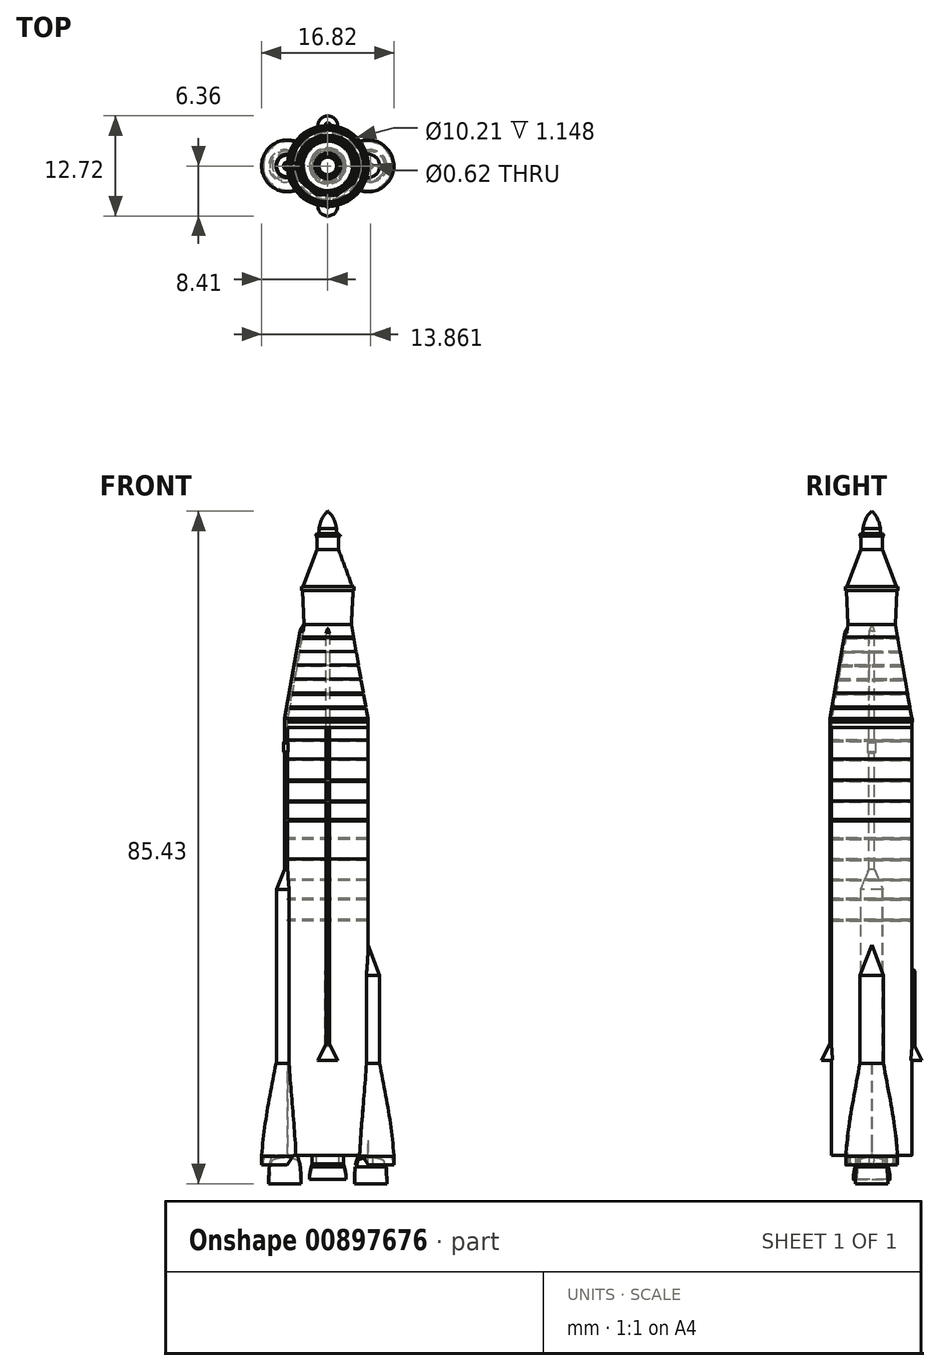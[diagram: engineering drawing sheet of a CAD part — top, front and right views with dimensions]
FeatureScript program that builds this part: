
annotation { "Feature Type Name" : "Feature", "Feature Type Description" : "" }
export const myFeature = defineFeature(function(context is Context, id is Id, definition is map)
    precondition{}
    {
        {
            var Q0;
            Q0=qCreatedBy(makeId("Front.planeOp"),FACE);
            var sketch = newSketch(context, id + "F0", { "sketchPlane" : qUnion([Q0])});
            skFitSpline(sketch, "E0", {"points": [v(0, 33.25) * mm, v(-0.75, 32.29) * mm, v(-1.12, 31.04) * mm, v(-1.14, 31.02) * mm, v(-1.13, 31.02) * mm], "startDerivative": vector(-1.93, -1.75) * mm, "endDerivative": vector(0, -10.34) * mm});
            skLineSegment(sketch, "E1", {"start": v(-1.12, 31.04) * mm, "end": v(-1.12, 30.38) * mm});
            skLineSegment(sketch, "E2", {"start": v(-1.12, 30.38) * mm, "end": v(-1.36, 30.38) * mm});
            skLineSegment(sketch, "E3", {"start": v(-1.36, 30.38) * mm, "end": v(-1.62, 30.09) * mm});
            skLineSegment(sketch, "E4", {"start": v(-1.62, 30.09) * mm, "end": v(-1.36, 30.09) * mm});
            skLineSegment(sketch, "E5", {"start": v(-1.36, 30.09) * mm, "end": v(-1.36, 28.36) * mm});
            skLineSegment(sketch, "E6", {"start": v(-1.36, 28.36) * mm, "end": v(-3.13, 23.65) * mm});
            skLineSegment(sketch, "E7", {"start": v(-3.13, 23.65) * mm, "end": v(-3.34, 23.65) * mm});
            skLineSegment(sketch, "E8", {"start": v(-3.34, 23.65) * mm, "end": v(-3.34, 23.17) * mm});
            skLineSegment(sketch, "E9", {"start": v(-3.34, 23.17) * mm, "end": v(-3.22, 23.17) * mm});
            skLineSegment(sketch, "E10", {"start": v(-3.22, 23.17) * mm, "end": v(-3, 18.86) * mm});
            skLineSegment(sketch, "E11", {"start": v(-3, 18.86) * mm, "end": v(-5.1, 6.9) * mm});
            skLineSegment(sketch, "E12", {"start": v(-5.1, 6.9) * mm, "end": v(-5.1, -46.68) * mm});
            skLineSegment(sketch, "E13", {"start": v(0, 33.25) * mm, "end": v(0, -46.63) * mm});
            skLineSegment(sketch, "E14", {"start": v(0, -46.63) * mm, "end": v(0, -46.68) * mm});
            skLineSegment(sketch, "E15", {"start": v(0, -46.72) * mm, "end": v(0, -46.68) * mm});
            skLineSegment(sketch, "E16", {"start": v(0, -46.72) * mm, "end": v(0, -48.6) * mm});
            skLineSegment(sketch, "E17", {"start": v(0, -48.6) * mm, "end": v(-5.1, -48.6) * mm});
            skLineSegment(sketch, "E18", {"start": v(-5.1, -48.6) * mm, "end": v(-5.1, -46.69) * mm});
            skLineSegment(sketch, "E19", {"start": v(-5.1, -46.69) * mm, "end": v(-5.1, -46.68) * mm});
            skLineSegment(sketch, "E20", {"start": v(0, 0) * mm, "end": v(0, 54.61) * mm});
            skLineSegment(sketch, "E21", {"start": v(0, 54.61) * mm, "end": v(-49.9, 54.61) * mm});
            skLineSegment(sketch, "E22", {"start": v(-35.1, 47.93) * mm, "end": v(-34.7, 47.5) * mm});
            skLineSegment(sketch, "E23", {"start": v(50.7, 54.83) * mm, "end": v(50.65, 54.64) * mm});
            skLineSegment(sketch, "E24", {"start": v(-35.08, -48.61) * mm, "end": v(45, -48.61) * mm});
            skLineSegment(sketch, "E25", {"start": v(-35.08, -48.61) * mm, "end": v(-56.76, -48.61) * mm});
            skLineSegment(sketch, "E26", {"start": v(0, -46.68) * mm, "end": v(0, -48.61) * mm});
            skFitSpline(sketch, "E27", {"points": [v(-3.23, -48.61) * mm, v(-2.86, -45) * mm, v(-1.42, -36.8) * mm], "startDerivative": vector(0.63, 8.16) * mm, "endDerivative": vector(2.85, 15) * mm});
            skLineSegment(sketch, "E28", {"start": v(-1.42, -36.8) * mm, "end": v(0, -36.8) * mm});
            skLineSegment(sketch, "E29", {"start": v(0, -36.8) * mm, "end": v(0, -48.61) * mm});
            skLineSegment(sketch, "E30", {"start": v(-3.23, -48.61) * mm, "end": v(-3.23, -49.7) * mm});
            skLineSegment(sketch, "E31", {"start": v(-3.23, -49.7) * mm, "end": v(0, -49.7) * mm});
            skLineSegment(sketch, "E32", {"start": v(0, -49.7) * mm, "end": v(0, -49.67) * mm});
            skLineSegment(sketch, "E33", {"start": v(28.34, 54.64) * mm, "end": v(0, 54.64) * mm});
            skLineSegment(sketch, "E34", {"start": v(0, 54.64) * mm, "end": v(0, 0.05) * mm});
            skLineSegment(sketch, "E35", {"start": v(-21.54, 19.8) * mm, "end": v(2.52, 19.8) * mm});
            skLineSegment(sketch, "E36", {"start": v(-3.04, 19.8) * mm, "end": v(-3.13, 19.53) * mm});
            skLineSegment(sketch, "E37", {"start": v(-5.48, -12.23) * mm, "end": v(-5.48, 6.9) * mm});
            skLineSegment(sketch, "E38", {"start": v(-5.48, 6.9) * mm, "end": v(-3.37, 18.82) * mm});
            skLineSegment(sketch, "E39", {"start": v(-3.37, 18.82) * mm, "end": v(-3.13, 19.53) * mm});
            skLineSegment(sketch, "E40", {"start": v(-5.48, -12.23) * mm, "end": v(-6.5, -14.79) * mm});
            skLineSegment(sketch, "E41", {"start": v(-6.5, -14.79) * mm, "end": v(-6.5, -38.04) * mm});
            skLineSegment(sketch, "E42", {"start": v(-8.4, -49.8) * mm, "end": v(-5.14, -49.8) * mm});
            skLineSegment(sketch, "E43", {"start": v(-5.14, -49.8) * mm, "end": v(-4.4, -48.61) * mm});
            skLineSegment(sketch, "E44", {"start": v(-4.4, -48.61) * mm, "end": v(-5.1, -36.81) * mm});
            skLineSegment(sketch, "E45", {"start": v(-5.48, -12.23) * mm, "end": v(-5.1, -12.23) * mm});
            skLineSegment(sketch, "E46", {"start": v(-5.1, -36.81) * mm, "end": v(-5.14, -49.8) * mm});
            skLineSegment(sketch, "E47", {"start": v(-5.48, 6.9) * mm, "end": v(-5.1, 6.9) * mm});
            skLineSegment(sketch, "E48", {"start": v(-3.51, 18) * mm, "end": v(-3, 18.86) * mm});
            skLineSegment(sketch, "E49", {"start": v(-8.25, -49.8) * mm, "end": v(-8.18, -48.61) * mm});
            skLineSegment(sketch, "E50", {"start": v(-6.5, -38.04) * mm, "end": v(-5.1, -38.04) * mm});
            skFitSpline(sketch, "E51", {"points": [v(-8.4, -48.71) * mm, v(-8.04, -45.11) * mm, v(-6.6, -36.9) * mm], "startDerivative": vector(0.63, 8.16) * mm, "endDerivative": vector(2.85, 15) * mm});
            skLineSegment(sketch, "E52", {"start": v(-6.6, -36.9) * mm, "end": v(-5.17, -36.9) * mm});
            skLineSegment(sketch, "E53", {"start": v(-8.4, -48.71) * mm, "end": v(-8.4, -49.8) * mm});
            skLineSegment(sketch, "E54", {"start": v(-8.4, -49.8) * mm, "end": v(-5.17, -49.8) * mm});
            skLineSegment(sketch, "E55", {"start": v(-6.6, -36.9) * mm, "end": v(-6.5, -36) * mm});
            skLineSegment(sketch, "E56", {"start": v(-5.14, -49.8) * mm, "end": v(-5.14, -50.06) * mm});
            skLineSegment(sketch, "E57", {"start": v(-5.14, -50.06) * mm, "end": v(-1.45, -50.06) * mm});
            skLineSegment(sketch, "E58", {"start": v(-1.45, -50.06) * mm, "end": v(-1.45, -48.6) * mm});
            skFitSpline(sketch, "E59.MirrorCS", {"points": [v(8.4, -48.71) * mm, v(8.04, -45.11) * mm, v(6.6, -36.9) * mm], "startDerivative": vector(-0.63, 8.16) * mm, "endDerivative": vector(-2.85, 15) * mm});
            skLineSegment(sketch, "E60.MirrorCS", {"start": v(8.4, -48.71) * mm, "end": v(8.4, -49.8) * mm});
            skLineSegment(sketch, "E61.MirrorCS", {"start": v(8.4, -49.8) * mm, "end": v(5.14, -49.8) * mm});
            skLineSegment(sketch, "E62.MirrorCS", {"start": v(5.1, 6.9) * mm, "end": v(5.1, -46.68) * mm});
            skLineSegment(sketch, "E63", {"start": v(6.6, -36.9) * mm, "end": v(6.6, -25.72) * mm});
            skLineSegment(sketch, "E64", {"start": v(6.6, -25.72) * mm, "end": v(5.1, -21.85) * mm});
            skLineSegment(sketch, "E65", {"start": v(5.14, -49.8) * mm, "end": v(5.1, -46.68) * mm});
            skLineSegment(sketch, "E66.MirrorCS", {"start": v(8.25, -49.8) * mm, "end": v(8.18, -48.61) * mm});
            skLineSegment(sketch, "E67.MirrorCS", {"start": v(5.14, -49.8) * mm, "end": v(4.4, -48.61) * mm});
            skLineSegment(sketch, "E68.MirrorCS", {"start": v(5.14, -50.06) * mm, "end": v(1.45, -50.06) * mm});
            skLineSegment(sketch, "E69.MirrorCS", {"start": v(5.14, -49.8) * mm, "end": v(5.14, -50.06) * mm});
            skLineSegment(sketch, "E70.MirrorCS", {"start": v(1.45, -50.06) * mm, "end": v(1.45, -48.6) * mm});
            skLineSegment(sketch, "E71", {"start": v(3.4, -52.18) * mm, "end": v(7.5, -52.18) * mm});
            skFitSpline(sketch, "E72", {"points": [v(3.4, -52.18) * mm, v(3.46, -50.24) * mm, v(3.65, -49.24) * mm, v(3.86, -48.61) * mm, v(3.86, -48.61) * mm], "startDerivative": vector(0.05, 4.96) * mm, "endDerivative": vector(0.02, -0.01) * mm});
            skLineSegment(sketch, "E73", {"start": v(5.45, -52.18) * mm, "end": v(5.45, -48.61) * mm});
            skFitSpline(sketch, "E74", {"points": [v(3.59, -52.18) * mm, v(3.65, -50.23) * mm, v(3.81, -49.3) * mm, v(3.9, -49.17) * mm], "startDerivative": vector(0.01, 4.02) * mm, "endDerivative": vector(0.64, 0.62) * mm});
            skFitSpline(sketch, "E75", {"points": [v(3.9, -49.17) * mm, v(4.06, -49.08) * mm, v(4.96, -48.85) * mm, v(5.45, -48.82) * mm, v(5.45, -48.82) * mm], "startDerivative": vector(0.6, 0.45) * mm, "endDerivative": vector(-0.02, -0.05) * mm});
            skLineSegment(sketch, "E76", {"start": v(3.86, -48.61) * mm, "end": v(8.4, -48.61) * mm});
            skLineSegment(sketch, "E77.MirrorCS", {"start": v(-5.45, -52.18) * mm, "end": v(-5.45, -48.61) * mm});
            skFitSpline(sketch, "E78.MirrorCS", {"points": [v(-3.4, -52.18) * mm, v(-3.46, -50.24) * mm, v(-3.65, -49.24) * mm, v(-3.86, -48.61) * mm, v(-3.86, -48.61) * mm], "startDerivative": vector(-0.05, 4.96) * mm, "endDerivative": vector(-0.02, -0.01) * mm});
            skFitSpline(sketch, "E79.MirrorCS", {"points": [v(-3.59, -52.18) * mm, v(-3.65, -50.23) * mm, v(-3.81, -49.3) * mm, v(-3.9, -49.17) * mm], "startDerivative": vector(-0.01, 4.02) * mm, "endDerivative": vector(-0.64, 0.62) * mm});
            skLineSegment(sketch, "E80.MirrorCS", {"start": v(-3.4, -52.18) * mm, "end": v(-7.5, -52.18) * mm});
            skFitSpline(sketch, "E81.MirrorCS", {"points": [v(-3.9, -49.17) * mm, v(-4.06, -49.08) * mm, v(-4.96, -48.85) * mm, v(-5.45, -48.82) * mm, v(-5.45, -48.82) * mm], "startDerivative": vector(-0.6, 0.45) * mm, "endDerivative": vector(0.02, -0.05) * mm});
            skLineSegment(sketch, "E82", {"start": v(1.98, -48.61) * mm, "end": v(1.98, -49.64) * mm});
            skLineSegment(sketch, "E83", {"start": v(-1.84, -51.64) * mm, "end": v(2.34, -51.64) * mm});
            skFitSpline(sketch, "E84", {"points": [v(1.98, -49.64) * mm, v(2.06, -49.88) * mm, v(2.26, -50.7) * mm, v(2.34, -51.64) * mm], "startDerivative": vector(0.37, -0.95) * mm, "endDerivative": vector(0.09, -2.27) * mm});
            skFitSpline(sketch, "E85", {"points": [v(2.26, -51.64) * mm, v(2.25, -51.34) * mm, v(2.08, -50.5) * mm, v(1.67, -49.82) * mm, v(0, -49.4) * mm], "startDerivative": vector(0.02, 1.75) * mm, "endDerivative": vector(-5.55, 0.73) * mm});
            skLineSegment(sketch, "E86", {"start": v(0, -48.26) * mm, "end": v(0, -55.58) * mm});
            skLineSegment(sketch, "E87", {"start": v(0, -49.4) * mm, "end": v(0, -49.4) * mm});
            skLineSegment(sketch, "E88", {"start": v(-5.1, 3.49) * mm, "end": v(-5.73, 3.49) * mm});
            skLineSegment(sketch, "E89", {"start": v(-5.73, 2.7) * mm, "end": v(-5.1, 2.7) * mm});
            skLineSegment(sketch, "E90", {"start": v(-5.62, 3.49) * mm, "end": v(-5.62, 2.7) * mm});
            skLineSegment(sketch, "E91", {"start": v(-5.62, 3.49) * mm, "end": v(-5.62, 3.8) * mm});
            skLineSegment(sketch, "E92", {"start": v(-5.62, 3.8) * mm, "end": v(-5.1, 3.8) * mm});
            skLineSegment(sketch, "E93", {"start": v(-5.62, 2.7) * mm, "end": v(-5.48, 2.44) * mm});
            skLineSegment(sketch, "E94", {"start": v(-5.62, 3.8) * mm, "end": v(-5.48, 4.03) * mm});
            skSolve(sketch);
        }
        {
            var Q0;
            Q0=qCreatedBy(makeId("Right.planeOp"),FACE);
            var sketch = newSketch(context, id + "F1", { "sketchPlane" : qUnion([Q0])});
            skLineSegment(sketch, "E95", {"start": v(50.7, 54.78) * mm, "end": v(50.64, 54.59) * mm});
            skLineSegment(sketch, "E96", {"start": v(-35.08, -48.66) * mm, "end": v(45, -48.66) * mm});
            skLineSegment(sketch, "E97", {"start": v(-35.08, -48.66) * mm, "end": v(-56.76, -48.66) * mm});
            skLineSegment(sketch, "E98", {"start": v(0, -46.73) * mm, "end": v(0, -48.66) * mm});
            skFitSpline(sketch, "E99", {"points": [v(-3.24, -48.66) * mm, v(-2.87, -45.06) * mm, v(-1.42, -36.84) * mm], "startDerivative": vector(0.63, 8.16) * mm, "endDerivative": vector(2.85, 15) * mm});
            skLineSegment(sketch, "E100", {"start": v(-1.42, -36.84) * mm, "end": v(0, -36.84) * mm});
            skLineSegment(sketch, "E101", {"start": v(0, -36.84) * mm, "end": v(0, -48.66) * mm});
            skLineSegment(sketch, "E102", {"start": v(0, -48.66) * mm, "end": v(0, -49.72) * mm});
            skLineSegment(sketch, "E103", {"start": v(-3.24, -48.66) * mm, "end": v(-3.24, -49.75) * mm});
            skLineSegment(sketch, "E104", {"start": v(-3.24, -49.75) * mm, "end": v(0, -49.75) * mm});
            skLineSegment(sketch, "E105", {"start": v(0, -49.75) * mm, "end": v(0, -49.72) * mm});
            skLineSegment(sketch, "E106", {"start": v(49.87, 54.6) * mm, "end": v(0, 54.6) * mm});
            skLineSegment(sketch, "E107", {"start": v(0, 54.6) * mm, "end": v(0, 0) * mm});
            skSolve(sketch);
        }
        {
            var Q0;
            {var subQ9=sQuery(id+"F0.wireOp",EDGE,"E11");Q0=makeQuery(id+"F0.imprint","IMPRINT",FACE,{"disambiguationData":[TD([[makeQuery(id+"F0.imprint","IMPRINT",EDGE,{"derivedFrom":subQ9}),1.0]])]});}
            var Q1;
            {var subQ1=sQuery(id+"F0.wireOp",EDGE,"E14");Q1=makeQuery(id+"F0.imprint","IMPRINT",FACE,{"disambiguationData":[TD([[makeQuery(id+"F0.imprint","IMPRINT",EDGE,{"derivedFrom":subQ1}),-1.0]])]});}
            var Q2;
            {var subQ6=sQuery(id+"F0.wireOp",EDGE,"E1");Q2=makeQuery(id+"F0.imprint","IMPRINT",FACE,{"disambiguationData":[TD([[makeQuery(id+"F0.imprint","IMPRINT",EDGE,{"derivedFrom":subQ6}),1.0]])]});}
            var Q3;
            {var subQ0=sQuery(id+"F0.wireOp",EDGE,"E18");Q3=makeQuery(id+"F0.imprint","IMPRINT",FACE,{"disambiguationData":[TD([[makeQuery(id+"F0.imprint","IMPRINT",EDGE,{"derivedFrom":subQ0}),-1.0]])]});}
            var Q4;
            Q4=sQuery(id+"F0.wireOp",EDGE,"E13");
            revolve(context, id + "F2", {"surfaceOperationType" : NewSurfaceOperationType.NEW, "entities" : qUnion([Q0, Q1, Q2, Q3]), "axis" : qUnion([Q4]), "revolveType" : RevolveType.FULL});
        }
        {
            var Q0;
            {var subQ5=sQuery(id+"F0.wireOp",EDGE,"E24");var subQ6=makeQuery(id+"F0.imprint","INTERSECT",VERTEX,{"derivedFrom":[subQ5,sQuery(id+"F0.wireOp",EDGE,"E49")]});Q0=makeQuery(id+"F0.imprint","IMPRINT",FACE,{"disambiguationData":[TD([[makeQuery(id+"F0.imprint","IMPRINT",EDGE,{"disambiguationData":[TD([[subQ6,1.0]])],"derivedFrom":subQ5}),1.0]])]});}
            var Q1;
            {var subQ3=sQuery(id+"F0.wireOp",EDGE,"E40");Q1=makeQuery(id+"F0.imprint","IMPRINT",FACE,{"disambiguationData":[TD([[makeQuery(id+"F0.imprint","IMPRINT",EDGE,{"derivedFrom":subQ3}),1.0]])]});}
            var Q2;
            {var subQ4=sQuery(id+"F0.wireOp",EDGE,"E49");Q2=makeQuery(id+"F0.imprint","IMPRINT",FACE,{"disambiguationData":[TD([[makeQuery(id+"F0.imprint","IMPRINT",EDGE,{"derivedFrom":subQ4}),1.0]])]});}
            var Q3;
            {var subQ5=sQuery(id+"F0.wireOp",EDGE,"eI0OFrzm-inzm-73C8-oKcD-yxVDyEnJwxOV");Q3=makeQuery(id+"F0.imprint","IMPRINT",FACE,{"disambiguationData":[TD([[makeQuery(id+"F0.imprint","IMPRINT",EDGE,{"derivedFrom":subQ5}),1.0]])]});}
            var Q4;
            {var subQ5=sQuery(id+"F0.wireOp",EDGE,"E90");Q4=makeQuery(id+"F0.imprint","IMPRINT",FACE,{"disambiguationData":[TD([[makeQuery(id+"F0.imprint","IMPRINT",EDGE,{"derivedFrom":subQ5}),1.0]])]});}
            var Q5;
            {var subQ5=sQuery(id+"F0.wireOp",EDGE,"E91");Q5=makeQuery(id+"F0.imprint","IMPRINT",FACE,{"disambiguationData":[TD([[makeQuery(id+"F0.imprint","IMPRINT",EDGE,{"derivedFrom":subQ5}),-1.0]])]});}
            var Q6;
            {var subQ0=sQuery(id+"F0.wireOp",EDGE,"E47");Q6=makeQuery(id+"F0.imprint","IMPRINT",FACE,{"disambiguationData":[TD([[makeQuery(id+"F0.imprint","IMPRINT",EDGE,{"derivedFrom":subQ0}),-1.0]])]});}
            var Q7;
            {var subQ0=sQuery(id+"F0.wireOp",EDGE,"E45");Q7=makeQuery(id+"F0.imprint","IMPRINT",FACE,{"disambiguationData":[TD([[makeQuery(id+"F0.imprint","IMPRINT",EDGE,{"derivedFrom":subQ0}),1.0]])]});}
            var Q8;
            {var subQ0=sQuery(id+"F0.wireOp",EDGE,"E88");var subQ1=sQuery(id+"F0.wireOp",EDGE,"E12");var subQ2=makeQuery(id+"F0.imprint","INTERSECT",VERTEX,{"derivedFrom":[subQ1,subQ0]});Q8=makeQuery(id+"F0.imprint","IMPRINT",FACE,{"disambiguationData":[TD([[makeQuery(id+"F0.imprint","IMPRINT",EDGE,{"disambiguationData":[TD([[subQ2,-1.0]])],"derivedFrom":subQ1}),-1.0]])]});}
            var Q9;
            {var subQ0=sQuery(id+"F0.wireOp",EDGE,"E88");var subQ1=sQuery(id+"F0.wireOp",EDGE,"E12");var subQ2=makeQuery(id+"F0.imprint","INTERSECT",VERTEX,{"derivedFrom":[subQ1,subQ0]});Q9=makeQuery(id+"F0.imprint","IMPRINT",FACE,{"disambiguationData":[TD([[makeQuery(id+"F0.imprint","IMPRINT",EDGE,{"disambiguationData":[TD([[subQ2,1.0]])],"derivedFrom":subQ1}),-1.0]])]});}
            var Q10;
            {var subQ0=sQuery(id+"F0.wireOp",EDGE,"E94");Q10=makeQuery(id+"F0.imprint","IMPRINT",FACE,{"disambiguationData":[TD([[makeQuery(id+"F0.imprint","IMPRINT",EDGE,{"derivedFrom":subQ0}),-1.0]])]});}
            var Q11;
            {var subQ0=sQuery(id+"F0.wireOp",EDGE,"E93");Q11=makeQuery(id+"F0.imprint","IMPRINT",FACE,{"disambiguationData":[TD([[makeQuery(id+"F0.imprint","IMPRINT",EDGE,{"derivedFrom":subQ0}),1.0]])]});}
            var Q12;
            Q12=sQuery(id+"F0.wireOp",EDGE,"E12");
            revolve(context, id + "F3", {"operationType" : NewBodyOperationType.ADD, "surfaceOperationType" : NewSurfaceOperationType.NEW, "entities" : qUnion([Q0, Q1, Q2, Q3, Q4, Q5, Q6, Q7, Q8, Q9, Q10, Q11]), "axis" : qUnion([Q12]), "revolveType" : RevolveType.FULL});
        }
        {
            var Q0;
            Q0=qCreatedBy(makeId("Front.planeOp"),FACE);
            var sketch = newSketch(context, id + "F4", { "sketchPlane" : qUnion([Q0])});
            skLineSegment(sketch, "E108", {"start": v(-5.15, -49.8) * mm, "end": v(-4.38, -48.6) * mm});
            skLineSegment(sketch, "E109", {"start": v(-4.38, -48.6) * mm, "end": v(-1.71, -48.6) * mm});
            skLineSegment(sketch, "E110", {"start": v(-1.71, -48.6) * mm, "end": v(-1.71, -49.88) * mm});
            skLineSegment(sketch, "E111", {"start": v(-1.71, -49.88) * mm, "end": v(-5.15, -49.8) * mm});
            skLineSegment(sketch, "E112", {"start": v(-5.15, -49.8) * mm, "end": v(-5.15, -49.89) * mm});
            skLineSegment(sketch, "E113", {"start": v(-5.15, -49.89) * mm, "end": v(-1.71, -49.88) * mm});
            skSolve(sketch);
        }
        {
            var Q0;
            Q0 = qSketchRegion(id + "F4", true);
            extrude(context, id + "F5", {"entities" : qUnion([Q0]), "operationType" : NewBodyOperationType.REMOVE, "depth" : 10.24 * mm, "offsetDistance" : 25.4 * mm, "hasSecondDirection" : true, "secondDirectionOppositeDirection" : true, "secondDirectionDepth" : 25.4 * mm});
        }
        {
            var Q0;
            {var subQ4=sQuery(id+"F0.wireOp",EDGE,"E63");Q0=makeQuery(id+"F0.imprint","IMPRINT",FACE,{"disambiguationData":[TD([[makeQuery(id+"F0.imprint","IMPRINT",EDGE,{"derivedFrom":subQ4}),1.0]])]});}
            var Q1;
            {var subQ0=sQuery(id+"F0.wireOp",EDGE,"E60.MirrorCS");Q1=makeQuery(id+"F0.imprint","IMPRINT",FACE,{"disambiguationData":[TD([[makeQuery(id+"F0.imprint","IMPRINT",EDGE,{"derivedFrom":subQ0}),-1.0]])]});}
            var Q2;
            Q2=sQuery(id+"F0.wireOp",EDGE,"E62.MirrorCS");
            revolve(context, id + "F6", {"operationType" : NewBodyOperationType.ADD, "surfaceOperationType" : NewSurfaceOperationType.NEW, "entities" : qUnion([Q0, Q1]), "axis" : qUnion([Q2]), "revolveType" : RevolveType.FULL});
        }
        {
            var Q0;
            {var subQ1=sQuery(id+"F0.wireOp",EDGE,"E67.MirrorCS");Q0=makeQuery(id+"F0.imprint","IMPRINT",FACE,{"disambiguationData":[TD([[makeQuery(id+"F0.imprint","IMPRINT",EDGE,{"derivedFrom":subQ1}),1.0]])]});}
            var Q1;
            {var subQ5=sQuery(id+"F0.wireOp",EDGE,"E76");var subQ9=sQuery(id+"F0.wireOp",EDGE,"E67.MirrorCS");var subQ10=makeQuery(id+"F0.imprint","INTERSECT",VERTEX,{"derivedFrom":[subQ9,subQ5]});Q1=makeQuery(id+"F0.imprint","IMPRINT",FACE,{"disambiguationData":[TD([[makeQuery(id+"F0.imprint","IMPRINT",EDGE,{"disambiguationData":[TD([[subQ10,1.0]])],"derivedFrom":subQ9}),1.0]])]});}
            var Q2;
            {var subQ3=sQuery(id+"F0.wireOp",EDGE,"E70.MirrorCS");var subQ5=sQuery(id+"F0.wireOp",EDGE,"E68.MirrorCS");var subQ7=makeQuery(id+"F0.imprint","INTERSECT",VERTEX,{"derivedFrom":[subQ5,subQ3]});Q2=makeQuery(id+"F0.imprint","IMPRINT",FACE,{"disambiguationData":[TD([[makeQuery(id+"F0.imprint","IMPRINT",EDGE,{"disambiguationData":[TD([[subQ7,1.0]])],"derivedFrom":subQ5}),-1.0]])]});}
            var Q3;
            {var subQ0=sQuery(id+"F0.wireOp",EDGE,"E82");Q3=makeQuery(id+"F0.imprint","IMPRINT",FACE,{"disambiguationData":[TD([[makeQuery(id+"F0.imprint","IMPRINT",EDGE,{"derivedFrom":subQ0}),1.0]])]});}
            var Q4;
            {var subQ0=sQuery(id+"F0.wireOp",EDGE,"E82");Q4=makeQuery(id+"F0.imprint","IMPRINT",FACE,{"disambiguationData":[TD([[makeQuery(id+"F0.imprint","IMPRINT",EDGE,{"derivedFrom":subQ0}),-1.0]])]});}
            extrude(context, id + "F7", {"entities" : qUnion([Q0, Q1, Q2, Q3, Q4]), "operationType" : NewBodyOperationType.REMOVE, "oppositeDirection" : true, "depth" : 25.4 * mm, "offsetDistance" : 25.4 * mm, "hasSecondDirection" : true, "secondDirectionOppositeDirection" : false, "secondDirectionDepth" : 25.93 * mm});
        }
        {
            var Q0;
            {var subQ0=sQuery(id+"F0.wireOp",EDGE,"E76");var subQ1=sQuery(id+"F0.wireOp",EDGE,"E65");var subQ2=makeQuery(id+"F0.imprint","INTERSECT",VERTEX,{"derivedFrom":[subQ1,subQ0]});Q0=makeQuery(id+"F0.imprint","IMPRINT",FACE,{"disambiguationData":[TD([[makeQuery(id+"F0.imprint","IMPRINT",EDGE,{"disambiguationData":[TD([[subQ2,1.0]])],"derivedFrom":subQ1}),-1.0]])]});}
            var Q1;
            {var subQ0=sQuery(id+"F0.wireOp",EDGE,"E76");var subQ1=sQuery(id+"F0.wireOp",EDGE,"E65");var subQ2=makeQuery(id+"F0.imprint","INTERSECT",VERTEX,{"derivedFrom":[subQ1,subQ0]});Q1=makeQuery(id+"F0.imprint","IMPRINT",FACE,{"disambiguationData":[TD([[makeQuery(id+"F0.imprint","IMPRINT",EDGE,{"disambiguationData":[TD([[subQ2,1.0]])],"derivedFrom":subQ1}),1.0]])]});}
            var Q2;
            {var subQ5=sQuery(id+"F0.wireOp",EDGE,"E76");var subQ9=sQuery(id+"F0.wireOp",EDGE,"E67.MirrorCS");var subQ10=makeQuery(id+"F0.imprint","INTERSECT",VERTEX,{"derivedFrom":[subQ9,subQ5]});Q2=makeQuery(id+"F0.imprint","IMPRINT",FACE,{"disambiguationData":[TD([[makeQuery(id+"F0.imprint","IMPRINT",EDGE,{"disambiguationData":[TD([[subQ10,1.0]])],"derivedFrom":subQ9}),1.0]])]});}
            var Q3;
            {var subQ0=sQuery(id+"F0.wireOp",EDGE,"E72");var subQ1=sQuery(id+"F0.wireOp",EDGE,"E68.MirrorCS");var subQ2=makeQuery(id+"F0.imprint","INTERSECT",VERTEX,{"derivedFrom":[subQ1,subQ0]});Q3=makeQuery(id+"F0.imprint","IMPRINT",FACE,{"disambiguationData":[TD([[makeQuery(id+"F0.imprint","IMPRINT",EDGE,{"disambiguationData":[TD([[subQ2,1.0]])],"derivedFrom":subQ1}),1.0]])]});}
            var Q4;
            Q4=sQuery(id+"F0.wireOp",EDGE,"E73");
            revolve(context, id + "F8", {"operationType" : NewBodyOperationType.ADD, "surfaceOperationType" : NewSurfaceOperationType.NEW, "entities" : qUnion([Q0, Q1, Q2, Q3]), "axis" : qUnion([Q4]), "revolveType" : RevolveType.FULL});
        }
        {
            var Q0;
            Q0=makeQuery(id+"F0.imprint","IMPRINT",FACE,{"disambiguationData":[TD([[makeQuery(id+"F0.imprint","IMPRINT",EDGE,{"derivedFrom":sQuery(id+"F0.wireOp",EDGE,"E11")}),-1.0]])]});
            var Q1;
            Q1=sQuery(id+"F0.wireOp",EDGE,"E11");
            revolve(context, id + "F9", {"operationType" : NewBodyOperationType.ADD, "surfaceOperationType" : NewSurfaceOperationType.NEW, "entities" : qUnion([Q0]), "axis" : qUnion([Q1]), "revolveType" : RevolveType.FULL});
        }
        {
            var Q0;
            {var subQ0=sQuery(id+"F0.wireOp",EDGE,"E77.MirrorCS");var subQ1=sQuery(id+"F0.wireOp",EDGE,"E24");var subQ2=makeQuery(id+"F0.imprint","INTERSECT",VERTEX,{"derivedFrom":[subQ1,subQ0]});Q0=makeQuery(id+"F0.imprint","IMPRINT",FACE,{"disambiguationData":[TD([[makeQuery(id+"F0.imprint","IMPRINT",EDGE,{"disambiguationData":[TD([[subQ2,-1.0]])],"derivedFrom":subQ1}),-1.0]])]});}
            var Q1;
            {var subQ1=sQuery(id+"F0.wireOp",EDGE,"E24");var subQ3=sQuery(id+"F0.wireOp",EDGE,"E46");var subQ4=makeQuery(id+"F0.imprint","INTERSECT",VERTEX,{"derivedFrom":[subQ1,subQ3]});Q1=makeQuery(id+"F0.imprint","IMPRINT",FACE,{"disambiguationData":[TD([[makeQuery(id+"F0.imprint","IMPRINT",EDGE,{"disambiguationData":[TD([[subQ4,-1.0]])],"derivedFrom":subQ3}),1.0]])]});}
            var Q2;
            {var subQ0=sQuery(id+"F0.wireOp",EDGE,"E78.MirrorCS");var subQ1=sQuery(id+"F0.wireOp",EDGE,"E57");var subQ2=makeQuery(id+"F0.imprint","INTERSECT",VERTEX,{"derivedFrom":[subQ1,subQ0]});Q2=makeQuery(id+"F0.imprint","IMPRINT",FACE,{"disambiguationData":[TD([[makeQuery(id+"F0.imprint","IMPRINT",EDGE,{"disambiguationData":[TD([[subQ2,1.0]])],"derivedFrom":subQ1}),1.0]])]});}
            var Q3;
            {var subQ0=sQuery(id+"F0.wireOp",EDGE,"E78.MirrorCS");var subQ1=sQuery(id+"F0.wireOp",EDGE,"E57");var subQ2=makeQuery(id+"F0.imprint","INTERSECT",VERTEX,{"derivedFrom":[subQ1,subQ0]});Q3=makeQuery(id+"F0.imprint","IMPRINT",FACE,{"disambiguationData":[TD([[makeQuery(id+"F0.imprint","IMPRINT",EDGE,{"disambiguationData":[TD([[subQ2,1.0]])],"derivedFrom":subQ1}),-1.0]])]});}
            var Q4;
            Q4=sQuery(id+"F0.wireOp",EDGE,"E77.MirrorCS");
            revolve(context, id + "F10", {"operationType" : NewBodyOperationType.ADD, "surfaceOperationType" : NewSurfaceOperationType.NEW, "entities" : qUnion([Q0, Q1, Q2, Q3]), "axis" : qUnion([Q4]), "revolveType" : RevolveType.FULL});
        }
        {
            var Q0;
            {var subQ0=sQuery(id+"F0.wireOp",EDGE,"E82");Q0=makeQuery(id+"F0.imprint","IMPRINT",FACE,{"disambiguationData":[TD([[makeQuery(id+"F0.imprint","IMPRINT",EDGE,{"derivedFrom":subQ0}),-1.0]])]});}
            var Q1;
            {var subQ0=sQuery(id+"F0.wireOp",EDGE,"E84");var subQ1=sQuery(id+"F0.wireOp",EDGE,"E68.MirrorCS");var subQ2=makeQuery(id+"F0.imprint","INTERSECT",VERTEX,{"derivedFrom":[subQ1,subQ0]});Q1=makeQuery(id+"F0.imprint","IMPRINT",FACE,{"disambiguationData":[TD([[makeQuery(id+"F0.imprint","IMPRINT",EDGE,{"disambiguationData":[TD([[subQ2,-1.0]])],"derivedFrom":subQ1}),1.0]])]});}
            var Q2;
            Q2=sQuery(id+"F0.wireOp",EDGE,"E86");
            revolve(context, id + "F11", {"operationType" : NewBodyOperationType.ADD, "surfaceOperationType" : NewSurfaceOperationType.NEW, "entities" : qUnion([Q0, Q1]), "axis" : qUnion([Q2]), "revolveType" : RevolveType.FULL});
        }
        {
            var Q0;
            Q0=qCreatedBy(makeId("Right.planeOp"),FACE);
            var sketch = newSketch(context, id + "F12", { "sketchPlane" : qUnion([Q0])});
            skLineSegment(sketch, "E114", {"start": v(5.1, 6.9) * mm, "end": v(5.1, -56.25) * mm});
            skLineSegment(sketch, "E115", {"start": v(5.1, -24.83) * mm, "end": v(5.83, -25.5) * mm});
            skLineSegment(sketch, "E116", {"start": v(5.47, -25.17) * mm, "end": v(5.47, -35.91) * mm});
            skLineSegment(sketch, "E117", {"start": v(5.47, -35.91) * mm, "end": v(6.13, -36.53) * mm});
            skLineSegment(sketch, "E118", {"start": v(6.13, -36.53) * mm, "end": v(5.1, -36.53) * mm});
            skPoint(sketch, "E119.endSnap0", {"position": v(5.62, -36.53) * mm});
            skLineSegment(sketch, "E120", {"start": v(5.47, -34.77) * mm, "end": v(6.36, -36.53) * mm});
            skLineSegment(sketch, "E121", {"start": v(6.13, -36.53) * mm, "end": v(6.36, -36.53) * mm});
            skLineSegment(sketch, "E122.MirrorCS", {"start": v(-5.47, -34.77) * mm, "end": v(-6.36, -36.53) * mm});
            skLineSegment(sketch, "E123.MirrorCS", {"start": v(-6.13, -36.53) * mm, "end": v(-5.1, -36.53) * mm});
            skLineSegment(sketch, "E124.MirrorCS", {"start": v(-6.13, -36.53) * mm, "end": v(-6.36, -36.53) * mm});
            skLineSegment(sketch, "E125", {"start": v(-5.47, 6.87) * mm, "end": v(-3.48, 17.83) * mm});
            skLineSegment(sketch, "E126", {"start": v(-3.48, 17.83) * mm, "end": v(-3.05, 18.49) * mm});
            skLineSegment(sketch, "E127", {"start": v(-3.05, 18.49) * mm, "end": v(-5.08, 6.9) * mm});
            skLineSegment(sketch, "E128", {"start": v(-5.08, 6.9) * mm, "end": v(-5.1, -36.53) * mm});
            skLineSegment(sketch, "E129", {"start": v(-5.47, 6.87) * mm, "end": v(-5.08, 6.9) * mm});
            skLineSegment(sketch, "E130", {"start": v(-5.47, -34.77) * mm, "end": v(-5.3, -34.44) * mm});
            skLineSegment(sketch, "E131", {"start": v(-5.3, -34.44) * mm, "end": v(-5.3, 6.89) * mm});
            skLineSegment(sketch, "E132", {"start": v(-5.3, 6.89) * mm, "end": v(-3.38, 17.83) * mm});
            skLineSegment(sketch, "E133", {"start": v(-3.38, 17.83) * mm, "end": v(-3.06, 18.4) * mm});
            skSolve(sketch);
        }
        {
            var Q0;
            {var subQ0=sQuery(id+"F12.wireOp",EDGE,"E117");Q0=makeQuery(id+"F12.imprint","IMPRINT",FACE,{"disambiguationData":[TD([[makeQuery(id+"F12.imprint","IMPRINT",EDGE,{"derivedFrom":subQ0}),-1.0]])]});}
            var Q1;
            {var subQ0=sQuery(id+"F12.wireOp",EDGE,"E117");Q1=makeQuery(id+"F12.imprint","IMPRINT",FACE,{"disambiguationData":[TD([[makeQuery(id+"F12.imprint","IMPRINT",EDGE,{"derivedFrom":subQ0}),1.0]])]});}
            var Q2;
            Q2=sQuery(id+"F12.wireOp",EDGE,"E114");
            revolve(context, id + "F13", {"operationType" : NewBodyOperationType.ADD, "surfaceOperationType" : NewSurfaceOperationType.NEW, "entities" : qUnion([Q0, Q1]), "axis" : qUnion([Q2]), "revolveType" : RevolveType.FULL});
        }
        {
            var Q0;
            {var subQ1=sQuery(id+"F12.wireOp",EDGE,"E122.MirrorCS");Q0=makeQuery(id+"F12.imprint","IMPRINT",FACE,{"disambiguationData":[TD([[makeQuery(id+"F12.imprint","IMPRINT",EDGE,{"derivedFrom":subQ1}),1.0]])]});}
            var Q1;
            Q1=sQuery(id+"F12.wireOp",EDGE,"E128");
            revolve(context, id + "F14", {"operationType" : NewBodyOperationType.ADD, "surfaceOperationType" : NewSurfaceOperationType.NEW, "entities" : qUnion([Q0]), "axis" : qUnion([Q1]), "revolveType" : RevolveType.FULL});
        }
        {
            var Q0;
            {var subQ4=sQuery(id+"F12.wireOp",EDGE,"E132");Q0=makeQuery(id+"F12.imprint","IMPRINT",FACE,{"disambiguationData":[TD([[makeQuery(id+"F12.imprint","IMPRINT",EDGE,{"derivedFrom":subQ4}),-1.0]])]});}
            var Q1;
            Q1=sQuery(id+"F12.wireOp",EDGE,"E127");
            revolve(context, id + "F15", {"operationType" : NewBodyOperationType.ADD, "surfaceOperationType" : NewSurfaceOperationType.NEW, "entities" : qUnion([Q0]), "axis" : qUnion([Q1]), "revolveType" : RevolveType.FULL});
        }
        {
            var Q0;
            Q0=qCreatedBy(makeId("Right.planeOp"),FACE);
            var sketch = newSketch(context, id + "F16", { "sketchPlane" : qUnion([Q0])});
            skLineSegment(sketch, "E134", {"start": v(3.25, 17.43) * mm, "end": v(3.27, 17.43) * mm});
            skLineSegment(sketch, "E135", {"start": v(3.27, 17.43) * mm, "end": v(3.36, 16.91) * mm});
            skLineSegment(sketch, "E136", {"start": v(3.36, 16.91) * mm, "end": v(3.33, 16.9) * mm});
            skLineSegment(sketch, "E137", {"start": v(3.26, 17.36) * mm, "end": v(3.28, 17.36) * mm});
            skLineSegment(sketch, "E138", {"start": v(3.28, 17.36) * mm, "end": v(3.35, 16.98) * mm});
            skLineSegment(sketch, "E139", {"start": v(3.35, 16.98) * mm, "end": v(3.32, 16.98) * mm});
            skArc(sketch, "E140", {"start": v(3.3, 17.1) * mm, "mid": v(3.3, 17.19) * mm, "end": v(3.27, 17.27) * mm});
            skLineSegment(sketch, "E141", {"start": v(3.27, 17.27) * mm, "end": v(3.3, 17.1) * mm});
            skArc(sketch, "E142", {"start": v(3.62, 15.27) * mm, "mid": v(3.63, 15.36) * mm, "end": v(3.6, 15.45) * mm});
            skLineSegment(sketch, "E143", {"start": v(3.6, 15.45) * mm, "end": v(3.62, 15.27) * mm});
            skArc(sketch, "E144", {"start": v(3.93, 13.52) * mm, "mid": v(3.94, 13.62) * mm, "end": v(3.9, 13.7) * mm});
            skLineSegment(sketch, "E145", {"start": v(3.9, 13.7) * mm, "end": v(3.93, 13.52) * mm});
            skArc(sketch, "E146", {"start": v(4.25, 11.73) * mm, "mid": v(4.26, 11.82) * mm, "end": v(4.22, 11.9) * mm});
            skLineSegment(sketch, "E147", {"start": v(4.22, 11.9) * mm, "end": v(4.25, 11.73) * mm});
            skArc(sketch, "E148", {"start": v(4.57, 9.95) * mm, "mid": v(4.57, 10.05) * mm, "end": v(4.53, 10.13) * mm});
            skLineSegment(sketch, "E149", {"start": v(4.53, 10.13) * mm, "end": v(4.57, 9.95) * mm});
            skArc(sketch, "E150", {"start": v(4.88, 8.19) * mm, "mid": v(4.89, 8.28) * mm, "end": v(4.85, 8.37) * mm});
            skLineSegment(sketch, "E151", {"start": v(4.85, 8.37) * mm, "end": v(4.88, 8.19) * mm});
            skLineSegment(sketch, "E152", {"start": v(5.1, 6.91) * mm, "end": v(5.1, 5.75) * mm});
            skLineSegment(sketch, "E153", {"start": v(5.1, 5.75) * mm, "end": v(5.12, 5.75) * mm});
            skLineSegment(sketch, "E154", {"start": v(5.12, 5.75) * mm, "end": v(5.12, 6.91) * mm});
            skLineSegment(sketch, "E155", {"start": v(5.1, 6.9) * mm, "end": v(5.12, 6.9) * mm});
            skLineSegment(sketch, "E156", {"start": v(5.12, 6.9) * mm, "end": v(5.12, 6.9) * mm});
            skLineSegment(sketch, "E157", {"start": v(5.12, 6.9) * mm, "end": v(5.12, 5.75) * mm});
            skLineSegment(sketch, "E158", {"start": v(5.12, 5.75) * mm, "end": v(5.12, 5.75) * mm});
            skLineSegment(sketch, "E159", {"start": v(5.1, 6.46) * mm, "end": v(5.14, 6.46) * mm});
            skLineSegment(sketch, "E160", {"start": v(5.14, 6.46) * mm, "end": v(5.14, 6.9) * mm});
            skLineSegment(sketch, "E161", {"start": v(5.14, 6.9) * mm, "end": v(5.12, 6.9) * mm});
            skArc(sketch, "E162", {"start": v(5.1, 3.99) * mm, "mid": v(5.13, 4.08) * mm, "end": v(5.1, 4.17) * mm});
            skLineSegment(sketch, "E163", {"start": v(5.1, 4.17) * mm, "end": v(5.1, 3.99) * mm});
            skArc(sketch, "E164", {"start": v(5.1, 1.59) * mm, "mid": v(5.13, 1.68) * mm, "end": v(5.1, 1.77) * mm});
            skLineSegment(sketch, "E165", {"start": v(5.1, 1.77) * mm, "end": v(5.1, 1.59) * mm});
            skArc(sketch, "E166", {"start": v(5.1, -1.07) * mm, "mid": v(5.13, -0.98) * mm, "end": v(5.1, -0.88) * mm});
            skLineSegment(sketch, "E167", {"start": v(5.1, -0.88) * mm, "end": v(5.1, -1.07) * mm});
            skArc(sketch, "E168", {"start": v(5.1, -3.72) * mm, "mid": v(5.13, -3.62) * mm, "end": v(5.1, -3.53) * mm});
            skLineSegment(sketch, "E169", {"start": v(5.1, -3.53) * mm, "end": v(5.1, -3.72) * mm});
            skArc(sketch, "E170", {"start": v(5.1, -6.08) * mm, "mid": v(5.13, -6) * mm, "end": v(5.1, -5.9) * mm});
            skLineSegment(sketch, "E171", {"start": v(5.1, -5.9) * mm, "end": v(5.1, -6.08) * mm});
            skArc(sketch, "E172", {"start": v(5.1, -8.45) * mm, "mid": v(5.13, -8.36) * mm, "end": v(5.1, -8.27) * mm});
            skLineSegment(sketch, "E173", {"start": v(5.1, -8.27) * mm, "end": v(5.1, -8.45) * mm});
            skArc(sketch, "E174", {"start": v(5.1, -11.11) * mm, "mid": v(5.13, -11.02) * mm, "end": v(5.1, -10.93) * mm});
            skLineSegment(sketch, "E175", {"start": v(5.1, -10.93) * mm, "end": v(5.1, -11.11) * mm});
            skArc(sketch, "E176", {"start": v(5.1, -13.7) * mm, "mid": v(5.13, -13.6) * mm, "end": v(5.1, -13.5) * mm});
            skLineSegment(sketch, "E177", {"start": v(5.1, -13.5) * mm, "end": v(5.1, -13.7) * mm});
            skArc(sketch, "E178", {"start": v(5.1, -16.15) * mm, "mid": v(5.13, -16.06) * mm, "end": v(5.1, -15.97) * mm});
            skLineSegment(sketch, "E179", {"start": v(5.1, -15.97) * mm, "end": v(5.1, -16.15) * mm});
            skArc(sketch, "E180", {"start": v(5.1, -18.8) * mm, "mid": v(5.13, -18.7) * mm, "end": v(5.1, -18.62) * mm});
            skLineSegment(sketch, "E181", {"start": v(5.1, -18.62) * mm, "end": v(5.1, -18.8) * mm});
            skSolve(sketch);
        }
        {
            var Q0;
            {var subQ0=sQuery(id+"F16.wireOp",EDGE,"E140");Q0=makeQuery(id+"F16.imprint","IMPRINT",FACE,{"disambiguationData":[TD([[makeQuery(id+"F16.imprint","IMPRINT",EDGE,{"derivedFrom":subQ0}),1.0]])]});}
            var Q1;
            Q1=sQuery(id+"F0.wireOp",EDGE,"E13");
            revolve(context, id + "F17", {"surfaceOperationType" : NewSurfaceOperationType.NEW, "entities" : qUnion([Q0]), "axis" : qUnion([Q1]), "revolveType" : RevolveType.FULL});
        }
        {
            var Q0;
            Q0=makeQuery(id+"F16.imprint","IMPRINT",FACE,{"disambiguationData":[TD([[makeQuery(id+"F16.imprint","IMPRINT",EDGE,{"derivedFrom":sQuery(id+"F16.wireOp",EDGE,"E142")}),1.0]])]});
            var Q1;
            Q1=makeQuery(id+"F16.imprint","IMPRINT",FACE,{"disambiguationData":[TD([[makeQuery(id+"F16.imprint","IMPRINT",EDGE,{"derivedFrom":sQuery(id+"F16.wireOp",EDGE,"E144")}),1.0]])]});
            var Q2;
            Q2=makeQuery(id+"F16.imprint","IMPRINT",FACE,{"disambiguationData":[TD([[makeQuery(id+"F16.imprint","IMPRINT",EDGE,{"derivedFrom":sQuery(id+"F16.wireOp",EDGE,"E146")}),1.0]])]});
            var Q3;
            Q3=makeQuery(id+"F16.imprint","IMPRINT",FACE,{"disambiguationData":[TD([[makeQuery(id+"F16.imprint","IMPRINT",EDGE,{"derivedFrom":sQuery(id+"F16.wireOp",EDGE,"E148")}),1.0]])]});
            var Q4;
            Q4=makeQuery(id+"F16.imprint","IMPRINT",FACE,{"disambiguationData":[TD([[makeQuery(id+"F16.imprint","IMPRINT",EDGE,{"derivedFrom":sQuery(id+"F16.wireOp",EDGE,"E150")}),1.0]])]});
            var Q5;
            Q5=sQuery(id+"F1.wireOp",EDGE,"E107");
            revolve(context, id + "F18", {"surfaceOperationType" : NewSurfaceOperationType.NEW, "entities" : qUnion([Q0, Q1, Q2, Q3, Q4]), "axis" : qUnion([Q5]), "revolveType" : RevolveType.FULL});
        }
        {
            var Q0;
            Q0 = qSketchRegion(id + "F16", true);
            var Q1;
            Q1=sQuery(id+"F1.wireOp",EDGE,"E107");
            revolve(context, id + "F19", {"surfaceOperationType" : NewSurfaceOperationType.NEW, "entities" : qUnion([Q0]), "axis" : qUnion([Q1]), "revolveType" : RevolveType.FULL});
        }
    });
